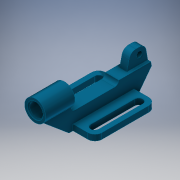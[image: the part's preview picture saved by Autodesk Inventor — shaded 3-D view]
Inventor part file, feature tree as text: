
AUTODESK INVENTOR PART (.ipt)
format: ipt  version: 2018.1 (Build 221151000, 151)  size: 202,240 bytes
history: native  units: in
note: dims shown in document units (in); Inventor stores cm internally (conversion verified against a paired STEP export)
features: sketch x6, extrude x4, fillet x3, revolve x1, hole x1
ambient origin geometry x8: Origin, YZ Plane, XZ Plane, XY Plane, X Axis, Y Axis, Z Axis, Center Point
bodies: Body1 (feature_tree)
feature tree (15):
  extrude  "Extrusion1"  Depth=0.23in
  fillet  "Fillet1"  Radius=0.133in
  extrude  "Extrusion2"  Depth=0.285in
  extrude  "Extrusion3"  Depth=0.44in TaperAngle=0.0deg
  fillet  "Fillet2"  Radius=0.44in
  extrude  "Extrusion4"  Depth=0.238in TaperAngle=0.0deg
  fillet  "Fillet3"  Radius=0.22in
  revolve  "Revolution1"  [1 undecoded]
  hole  "Hole2"  [1 undecoded]
  sketch  "Sketch1"  dims[d0=0.19in d1=0.0in d2=0.23in d3=0.133in]
  sketch  "Sketch2"  dims[d5=1.44in d6=0.285in]
  sketch  "Sketch3"  dims[d7=0.28in d8=0.435in d9=0.0in d10=0.44in d11=0.0in]
  sketch  "Sketch4"  dims[d12=0.13in d13=0.238in d14=0.0in d15=0.22in]
  sketch  "Sketch6"  dims[d27=0.125in d28=0.9587in]
  sketch  "Sketch7"  dims[d29=0.0856in d30=0.0394in d31=0.0394in d33=0.9587in d38=0.4858in d40=0.1834in d41=90.0deg d42=0.285in d43=0.2736in d44=0.189in d45=0.75in d46=0.375in d47=0.25in d48=0.5635in d49=1.0in d50=0.8108in]
note: 2 required parameter values undecoded (feature->parameter linkage not recoverable at this tier; creation-order binding heuristic only, values carry confidence <= 0.55)